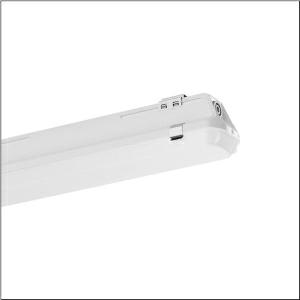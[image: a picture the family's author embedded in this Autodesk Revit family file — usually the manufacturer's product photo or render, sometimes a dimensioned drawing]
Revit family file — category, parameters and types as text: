
# Revit family: monsun_r__11_51fp20mp480h_c015
name_source: partatom
category: Lighting Fixtures
units: mm (PartAtom-declared; Revit-internal decimal feet)

## family parameters
Cut with Voids When Loaded = No
Host = Face
Light Source = No
Part Type = Normal
Room Calculation Point = No
Round Connector Dimension = Use Diameter
Shared = No

## types (1)
- --- (1 x LED, 8220 lm, 52.3 W, 4000K)
    Apparent Load = 52 VA
    CIE Flux Codes = 45 75 93 94 100
    Color Rendering = 80
    Color Temperature = 4000K
    Default Elevation = 1800 mm
    Description = Monsun® 11, damp-proof luminaire, chain hanger, primary optical cover: enclosure, of PC, light emission: direct distribution, primary light characteristic: symmetric, installation type: suspended mounting, surface-mounted, horizontal mounting, vertical mounting, LED, rated luminous flux: 8.220lm, luminous efficacy: 157lm/W, light colour: 840, colour temperature: 4000K, control gear: ECG, with terminal, 3-pole, max. 2.5mm², mains connection: 220..240V, AC, 50/60Hz, rated input power: 52W, luminaire housing, of glass-fibre reinforced polyester, uncoated, bright grey, incl. chain hanger, length: 1.590mm, width: 90mm, height: 88mm, clip for enclosure, of stainless steel (V2A), ceiling mounting element, of stainless steel (V2A), chain hanger, of stainless steel (V2A), protection rating (complete): IP66, insulation class (complete): insulation class I (protective earthing), certification: CE, ENEC, VDE, UKCA, protection symbol: D, impact resistance: IK08, permissible operating ambient temperature: -35..+40°C, standard: EN 50419, EN 60598-2-1, no direct snow, no direct sun, no direct rain, for indoor or canopied outdoor use, corresponds to IFS (International Featured Standards) requirements for safety and quality in the food industry, contact your sales advisor before using the luminaires in applications with unclear chemical exposure, large temperature fluctuations or condensation-forming humidity, LABS conformity tested according to VDMA 24364:2018-05, packaging unit: 1 piece
    Height = 89 mm
    Lamp = 1 x LED
    Lamp Light Flux = 8220 lm
    Lamp Power = 52.3 W
    Lamp count = 1
    Length = 1590 mm
    Luminous efficacy = 157 lm/W
    Manufacturer = Siteco
    ModVariant = No
    Model = 51FP20MP480H
    Mounting Place = Ceiling
    Mounting Type = Surface mounted
    Number of Poles = 1
    OnlyDefault = Yes
    Power Factor = 1
    Product Name = Monsun® 11
    Product group = damp-proof luminaire
    ProductGroupID = 301
    Protection Class = Protection class I
    Protection Degree = IP 66
    RLX_Detail_Level = 1
    RLX_Emergency_Light_Flux = 0 lm
    RLX_Emergency_Type = 0
    RLX_Emergency_Type_DB = No
    RlxData = <blob elided: 89941 chars, md5=1b0c9d19>
    Socket = socket
    Standby Power = 0 W
    System Light Flux = 8220 lm
    System Power = 52 W
    Type Comments = factory setting: luminous flux: 100 % | (A | C | E) | 120 mA
    Type Image = l_1004748.jpg
    URL = http://relux.com
    VarID = @adj_156573
    Voltage = 0 V
    Weight = 0.00 kg
    Width = 90 mm

## geometry (parser evidence)
native form markers: Blend x4, Sweep x12
no freeform markers — native parametric forms only
